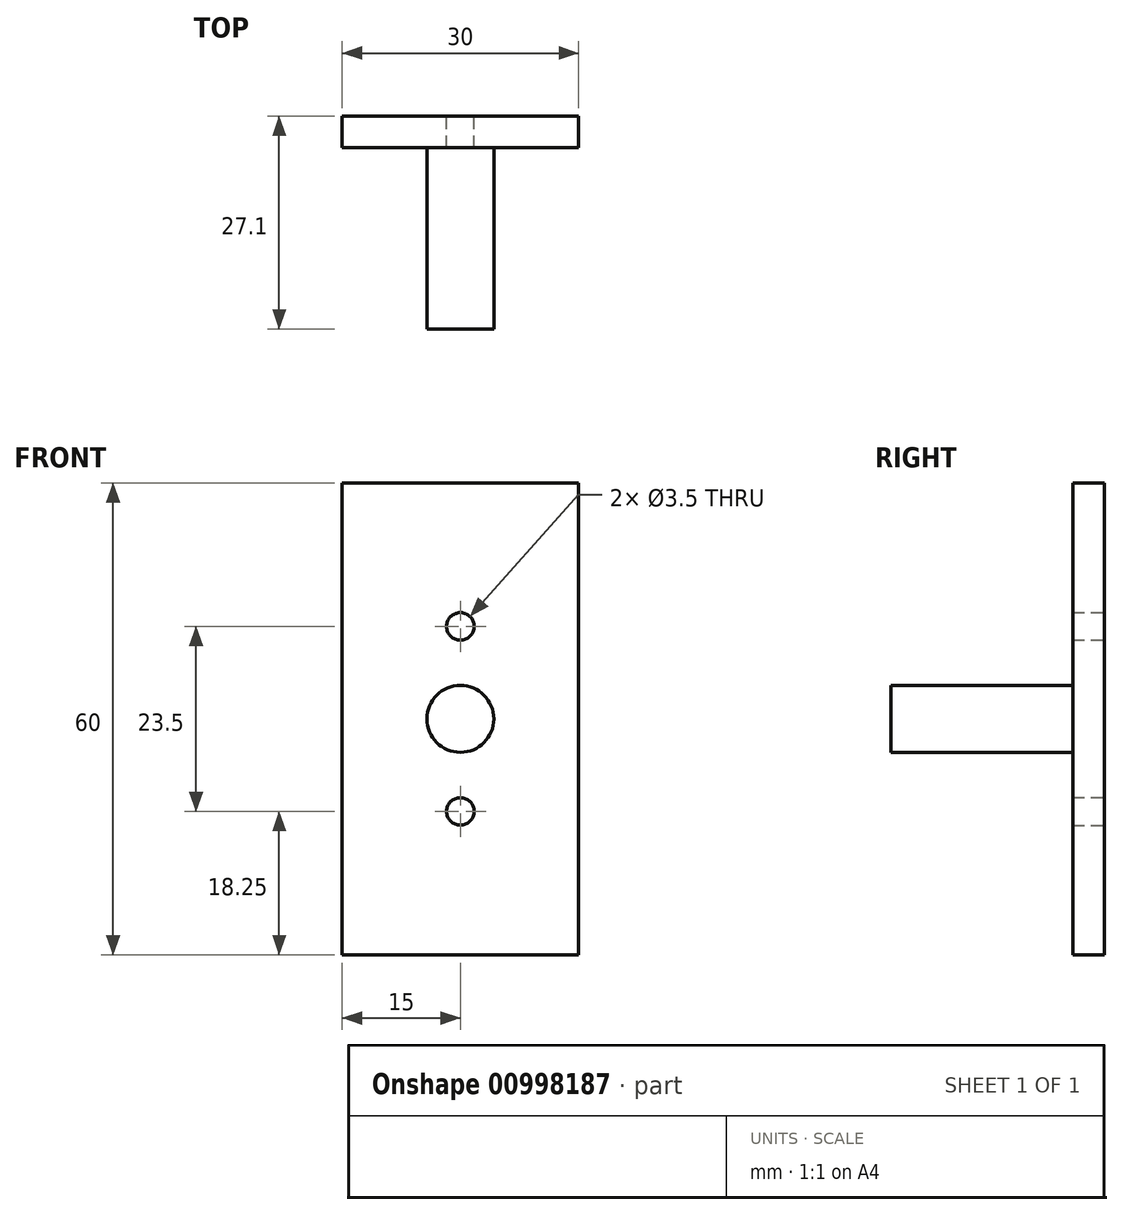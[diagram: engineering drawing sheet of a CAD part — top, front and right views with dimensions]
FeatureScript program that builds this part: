
annotation { "Feature Type Name" : "Feature", "Feature Type Description" : "" }
export const myFeature = defineFeature(function(context is Context, id is Id, definition is map)
    precondition{}
    {
        {
            var Q0;
            Q0=qCreatedBy(makeId("Front.planeOp"),FACE);
            var sketch = newSketch(context, id + "F0", { "sketchPlane" : qUnion([Q0])});
            skLineSegment(sketch, "E0", {"start": v(-15, 0) * mm, "end": v(-15, 30) * mm});
            skLineSegment(sketch, "E1", {"start": v(-15, 30) * mm, "end": v(0, 30) * mm});
            skLineSegment(sketch, "E2", {"start": v(0, 30) * mm, "end": v(15, 30) * mm});
            skLineSegment(sketch, "E3", {"start": v(15, 30) * mm, "end": v(15, 0) * mm});
            skLineSegment(sketch, "E4", {"start": v(15, 0) * mm, "end": v(15, -30) * mm});
            skLineSegment(sketch, "E5", {"start": v(15, -30) * mm, "end": v(0, -30) * mm});
            skLineSegment(sketch, "E6", {"start": v(0, -30) * mm, "end": v(-15, -30) * mm});
            skLineSegment(sketch, "E7", {"start": v(-15, -30) * mm, "end": v(-15, 0) * mm});
            skLineSegment(sketch, "E8", {"start": v(0, 0) * mm, "end": v(0, 11.75) * mm, "construction": true});
            skLineSegment(sketch, "E9", {"start": v(0, 0) * mm, "end": v(0, -11.75) * mm, "construction": true});
            skCircle(sketch, "E10", {"center": v(0, 11.75) * mm, "radius": 1.75 * mm});
            skCircle(sketch, "E11", {"center": v(0, -11.75) * mm, "radius": 1.75 * mm});
            skSolve(sketch);
        }
        {
            var Q0;
            Q0=makeQuery(id+"F0.imprint","IMPRINT",FACE,{"disambiguationData":[TD([[makeQuery(id+"F0.imprint","IMPRINT",EDGE,{"derivedFrom":sQuery(id+"F0.wireOp",EDGE,"E0")}),-1.0]])]});
            extrude(context, id + "F1", {"entities" : qUnion([Q0]), "depth" : 4 * mm, "offsetDistance" : 25 * mm});
        }
        {
            var Q0;
            Q0=makeQuery(id+"F1.opExtrude","CAP_FACE",FACE,{"disambiguationData":[OSD([sQuery(id+"F0.wireOp",EDGE,"E0"),sQuery(id+"F0.wireOp",EDGE,"E1"),sQuery(id+"F0.wireOp",EDGE,"E2"),sQuery(id+"F0.wireOp",EDGE,"E3"),sQuery(id+"F0.wireOp",EDGE,"E4"),sQuery(id+"F0.wireOp",EDGE,"E5"),sQuery(id+"F0.wireOp",EDGE,"E6"),sQuery(id+"F0.wireOp",EDGE,"E7"),sQuery(id+"F0.wireOp",EDGE,"E10"),sQuery(id+"F0.wireOp",EDGE,"E11")])],"isStart":false});
            var sketch = newSketch(context, id + "F2", { "sketchPlane" : qUnion([Q0])});
            skCircle(sketch, "E12", {"center": v(0, 0) * mm, "radius": 4.24 * mm});
            skSolve(sketch);
        }
        {
            var Q0;
            Q0=makeQuery(id+"F2.imprint","IMPRINT",FACE,{"disambiguationData":[TD([[makeQuery(id+"F2.imprint","IMPRINT",EDGE,{"derivedFrom":sQuery(id+"F2.wireOp",EDGE,"E12")}),1.0]])]});
            var sketch = newSketch(context, id + "F3", { "sketchPlane" : qUnion([Q0])});
            skSolve(sketch);
        }
        {
            var Q0;
            Q0=makeQuery(id+"F3.imprint","IMPRINT",FACE,{"disambiguationData":[TD([[makeQuery(id+"F3.imprint","IMPRINT",EDGE,{"derivedFrom":makeQuery(id+"F2.imprint","IMPRINT",EDGE,{"derivedFrom":sQuery(id+"F2.wireOp",EDGE,"E12")})}),1.0]])]});
            extrude(context, id + "F4", {"entities" : qUnion([Q0]), "operationType" : NewBodyOperationType.ADD, "depth" : 23.1 * mm, "offsetDistance" : 25 * mm});
        }
    });
